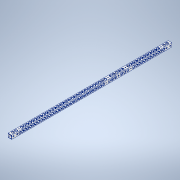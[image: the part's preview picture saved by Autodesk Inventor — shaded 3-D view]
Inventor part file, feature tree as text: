
AUTODESK INVENTOR PART (.ipt)
format: ipt  version: 2020.3 (Build 243373000, 373)  size: 433,664 bytes
history: native  units: mm
features: hole x10, sketch x10, other x1, extrude x1
ambient origin geometry x8: Origin, YZ Plane, XZ Plane, XY Plane, X Axis, Y Axis, Z Axis, Center Point
bodies: Body1 (feature_tree)
feature tree (22):
  other  "ソリッド1"
  extrude  "押し出し1"  Depth=15.0mm
  hole  "穴1"  [1 undecoded]
  hole  "穴2"  [1 undecoded]
  hole  "穴3"  [1 undecoded]
  hole  "穴4"  [1 undecoded]
  hole  "穴5"  [1 undecoded]
  hole  "穴6"  [1 undecoded]
  hole  "穴7"  [1 undecoded]
  hole  "穴8"  [1 undecoded]
  hole  "穴9"  [1 undecoded]
  hole  "穴10"  [1 undecoded]
  sketch  "スケッチ1"
  sketch  "スケッチ2"
  sketch  "スケッチ3"
  sketch  "スケッチ4"
  sketch  "スケッチ6"
  sketch  "スケッチ7"
  sketch  "スケッチ8"
  sketch  "スケッチ10"
  sketch  "スケッチ11"
  sketch  "スケッチ12"
note: 10 required parameter values undecoded (feature->parameter linkage not recoverable at this tier; creation-order binding heuristic only, values carry confidence <= 0.55)
